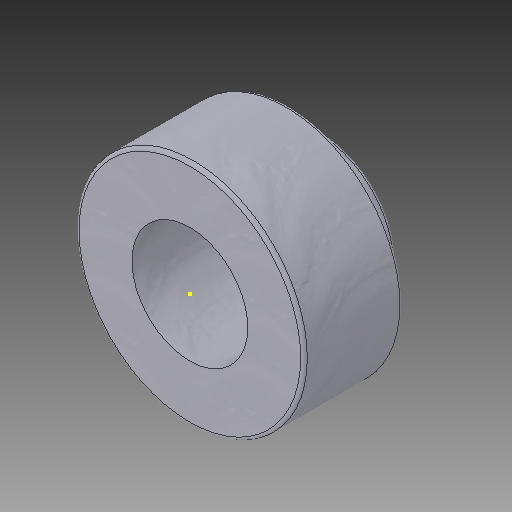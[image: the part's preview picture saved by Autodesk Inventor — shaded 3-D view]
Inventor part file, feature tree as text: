
AUTODESK INVENTOR PART (.ipt)
format: ipt  version: 2019 (Build 230136000, 136)  size: 206,336 bytes
history: native  units: in
note: dims shown in document units (in); Inventor stores cm internally (conversion verified against a paired STEP export)
features: sketch x6, other x3
ambient origin geometry x8: Origin, YZ Plane, XZ Plane, XY Plane, X Axis, Y Axis, Z Axis, Center Point
bodies: Solid1 (feature_tree)
feature tree (9):
  other  "project flange bearing part2_MIR1_MIR1.ipt"
  other  "Solid1::project flange bearing part2_MIR1_MIR1.ipt"
  other  "TaggingFeature1"
  sketch  "Sketch1"  dims[d0=0.3937in]
  sketch  "Sketch2"
  sketch  "Sketch3"
  sketch  "Sketch4"
  sketch  "Sketch5"
  sketch  "Sketch6"
